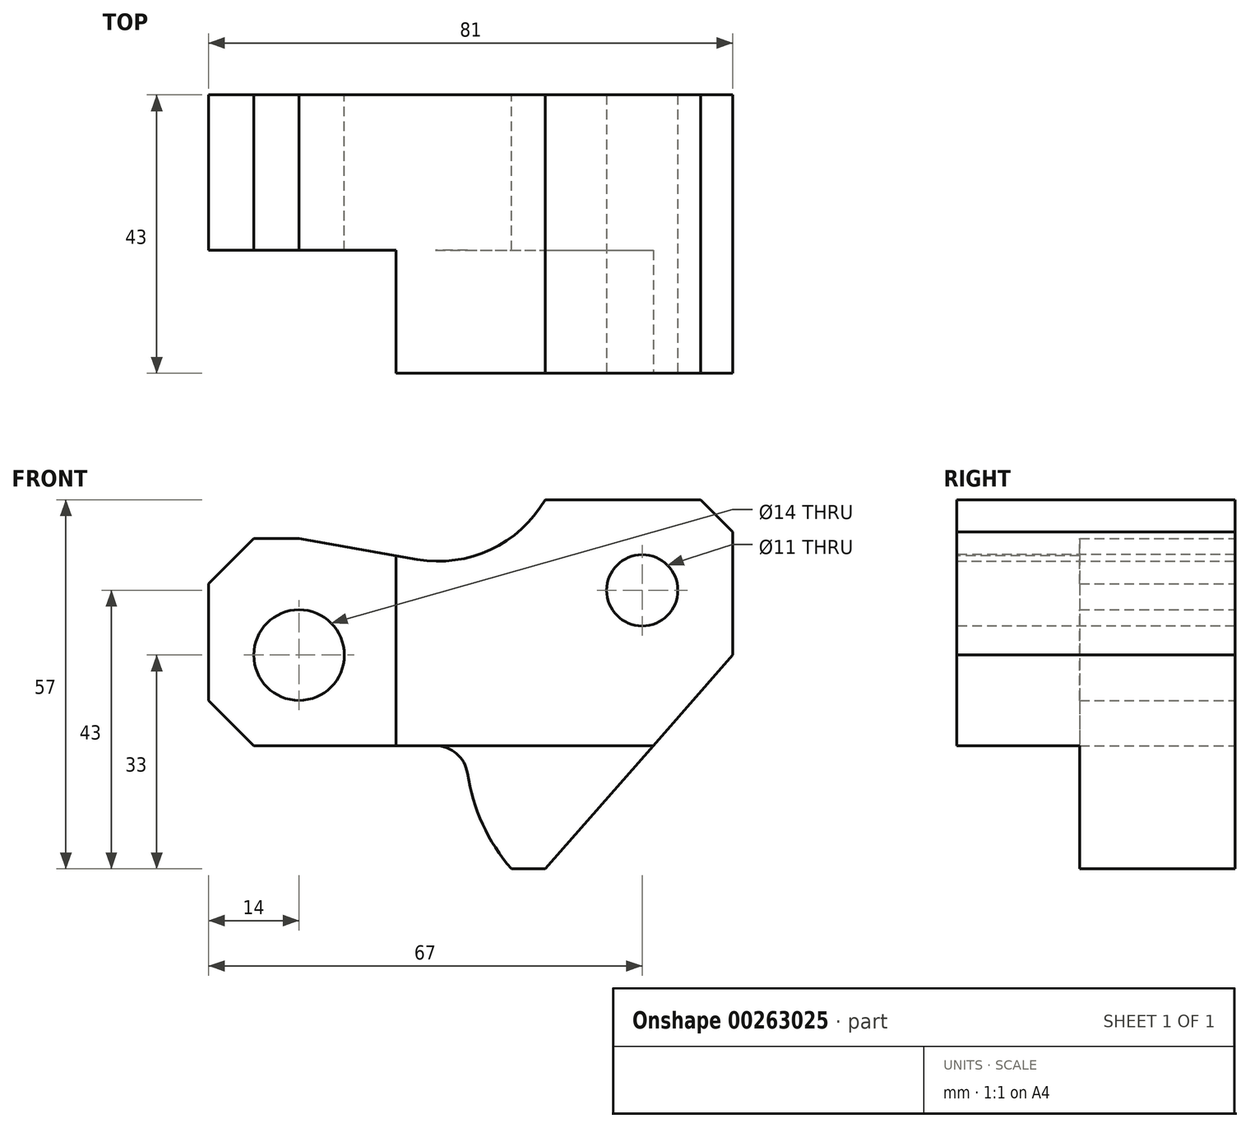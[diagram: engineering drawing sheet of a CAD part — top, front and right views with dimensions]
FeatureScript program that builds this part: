
annotation { "Feature Type Name" : "Feature", "Feature Type Description" : "" }
export const myFeature = defineFeature(function(context is Context, id is Id, definition is map)
    precondition{}
    {
        {
            var Q0;
            Q0=qCreatedBy(makeId("Front.planeOp"),FACE);
            var sketch = newSketch(context, id + "F0", { "sketchPlane" : qUnion([Q0])});
            skCircle(sketch, "E0", {"center": v(0, 0) * mm, "radius": 7 * mm});
            skLineSegment(sketch, "E1", {"start": v(-14, 11) * mm, "end": v(-14, -7) * mm});
            skLineSegment(sketch, "E2", {"start": v(-14, 11) * mm, "end": v(-7, 18) * mm});
            skLineSegment(sketch, "E3", {"start": v(-7, 18) * mm, "end": v(0, 18) * mm});
            skLineSegment(sketch, "E4", {"start": v(0, 18) * mm, "end": v(18.24, 14.78) * mm});
            skLineSegment(sketch, "E5", {"start": v(-14, -7) * mm, "end": v(-7, -14) * mm});
            skLineSegment(sketch, "E6", {"start": v(-7, -14) * mm, "end": v(21.07, -14) * mm});
            skArc(sketch, "E7", {"start": v(26.01, -18.26) * mm, "mid": v(24.33, -15.21) * mm, "end": v(21.07, -14) * mm});
            skArc(sketch, "E8", {"start": v(26.01, -18.26) * mm, "mid": v(28.35, -26.12) * mm, "end": v(32.79, -33) * mm});
            skLineSegment(sketch, "E9", {"start": v(32.79, -33) * mm, "end": v(38, -33) * mm});
            skLineSegment(sketch, "E10", {"start": v(38, -33) * mm, "end": v(67, 0) * mm});
            skLineSegment(sketch, "E11", {"start": v(67, 0) * mm, "end": v(67, 19) * mm});
            skLineSegment(sketch, "E12", {"start": v(67, 19) * mm, "end": v(62, 24) * mm});
            skLineSegment(sketch, "E13", {"start": v(62, 24) * mm, "end": v(38, 24) * mm});
            skArc(sketch, "E14", {"start": v(18.24, 14.78) * mm, "mid": v(29.57, 16.28) * mm, "end": v(38, 24) * mm});
            skLineSegment(sketch, "E15", {"start": v(-14, 11) * mm, "end": v(-14, 44.57) * mm, "construction": true});
            skLineSegment(sketch, "E16", {"start": v(-14, -7) * mm, "end": v(-14, -36.48) * mm, "construction": true});
            skLineSegment(sketch, "E17", {"start": v(67, 19) * mm, "end": v(67, 55.27) * mm, "construction": true});
            skLineSegment(sketch, "E18", {"start": v(0, 18) * mm, "end": v(19.15, 18) * mm, "construction": true});
            skSolve(sketch);
        }
        {
            var Q0;
            Q0 = qSketchRegion(id + "F0", true);
            extrude(context, id + "F1", {"entities" : qUnion([Q0]), "depth" : 43 * mm, "symmetric" : true});
        }
        {
            var Q0;
            Q0=makeQuery(id+"F1.opExtrude","CAP_FACE",FACE,{"disambiguationData":[OSD([sQuery(id+"F0.wireOp",EDGE,"E0"),sQuery(id+"F0.wireOp",EDGE,"E1"),sQuery(id+"F0.wireOp",EDGE,"E2"),sQuery(id+"F0.wireOp",EDGE,"E3"),sQuery(id+"F0.wireOp",EDGE,"E4"),sQuery(id+"F0.wireOp",EDGE,"E5"),sQuery(id+"F0.wireOp",EDGE,"E6"),sQuery(id+"F0.wireOp",EDGE,"E7"),sQuery(id+"F0.wireOp",EDGE,"E8"),sQuery(id+"F0.wireOp",EDGE,"E9"),sQuery(id+"F0.wireOp",EDGE,"E10"),sQuery(id+"F0.wireOp",EDGE,"E11"),sQuery(id+"F0.wireOp",EDGE,"E12"),sQuery(id+"F0.wireOp",EDGE,"E13"),sQuery(id+"F0.wireOp",EDGE,"E14")])],"isStart":false});
            var sketch = newSketch(context, id + "F2", { "sketchPlane" : qUnion([Q0])});
            skCircle(sketch, "E19", {"center": v(53, 10) * mm, "radius": 5.5 * mm});
            skLineSegment(sketch, "E20", {"start": v(15, 15.36) * mm, "end": v(15, -14) * mm});
            skLineSegment(sketch, "E21", {"start": v(15, -14) * mm, "end": v(54.7, -14) * mm});
            skLineSegment(sketch, "E22.0", {"start": v(0, 18) * mm, "end": v(18.24, 14.78) * mm});
            skPoint(sketch, "E23.0", {"position": v(-7, 18) * mm});
            skPoint(sketch, "E24.0", {"position": v(-14, 11) * mm});
            skPoint(sketch, "E25.0", {"position": v(-14, -7) * mm});
            skPoint(sketch, "E26.0", {"position": v(-7, -14) * mm});
            skLineSegment(sketch, "E27.0", {"start": v(-7, -14) * mm, "end": v(21.07, -14) * mm});
            skLineSegment(sketch, "E28", {"start": v(0, 18) * mm, "end": v(-7, 18) * mm});
            skLineSegment(sketch, "E29", {"start": v(-14, 11) * mm, "end": v(-14, -7) * mm});
            skLineSegment(sketch, "E30", {"start": v(-7, -14) * mm, "end": v(15, -14) * mm});
            skPoint(sketch, "E31.0", {"position": v(24.33, -15.21) * mm});
            skPoint(sketch, "E32.0", {"position": v(32.79, -33) * mm});
            skPoint(sketch, "E33.0", {"position": v(38, -33) * mm});
            skLineSegment(sketch, "E34.0", {"start": v(38, -33) * mm, "end": v(67, 0) * mm});
            skArc(sketch, "E35", {"start": v(26.01, -18.26) * mm, "mid": v(24.33, -15.21) * mm, "end": v(21.07, -14) * mm});
            skPoint(sketch, "E36.0", {"position": v(28.35, -26.12) * mm});
            skArc(sketch, "E37", {"start": v(26.01, -18.26) * mm, "mid": v(28.35, -26.12) * mm, "end": v(32.79, -33) * mm});
            skLineSegment(sketch, "E38", {"start": v(32.79, -33) * mm, "end": v(38, -33) * mm});
            skLineSegment(sketch, "E39", {"start": v(38, -33) * mm, "end": v(54.7, -14) * mm});
            skLineSegment(sketch, "E40", {"start": v(54.7, -14) * mm, "end": v(21.07, -14) * mm});
            skSolve(sketch);
        }
        {
            var Q0;
            Q0=makeQuery(id+"F2.imprint","IMPRINT",FACE,{"disambiguationData":[TD([[makeQuery(id+"F2.imprint","IMPRINT",EDGE,{"derivedFrom":sQuery(id+"F2.wireOp",EDGE,"E19")}),1.0]])]});
            var Q1;
            Q1=sQuery(id+"F2.wireOp",EDGE,"E19");
            extrude(context, id + "F3", {"entities" : qUnion([Q0]), "operationType" : NewBodyOperationType.REMOVE, "surfaceEntities" : qUnion([Q1]), "endBound" : BoundingType.THROUGH_ALL, "oppositeDirection" : true, "depth" : 25 * mm});
        }
        {
            var Q0;
            {var subQ2=sQuery(id+"F2.wireOp",EDGE,"E20");Q0=makeQuery(id+"F2.imprint","IMPRINT",FACE,{"disambiguationData":[TD([[makeQuery(id+"F2.imprint","IMPRINT",EDGE,{"derivedFrom":subQ2}),-1.0]])]});}
            var Q1;
            {var subQ2=sQuery(id+"F2.wireOp",EDGE,"E21");Q1=makeQuery(id+"F2.imprint","IMPRINT",FACE,{"disambiguationData":[TD([[makeQuery(id+"F2.imprint","IMPRINT",EDGE,{"derivedFrom":subQ2}),-1.0]])]});}
            extrude(context, id + "F4", {"entities" : qUnion([Q0, Q1]), "operationType" : NewBodyOperationType.REMOVE, "oppositeDirection" : true, "depth" : 19 * mm});
        }
        {
            var Q0;
            Q0=makeQuery(id+"F2.imprint","IMPRINT",FACE,{"disambiguationData":[TD([[makeQuery(id+"F2.imprint","IMPRINT",EDGE,{"derivedFrom":sQuery(id+"F2.wireOp",EDGE,"E19")}),-1.0]])]});
            cPlane(context, id + "F5", {"entities" : qUnion([Q0]), "cplaneType" : CPlaneType.OFFSET, "offset" : 19 * mm, "oppositeDirection" : true, "width" : 150 * mm, "height" : 150 * mm});
        }
    });
